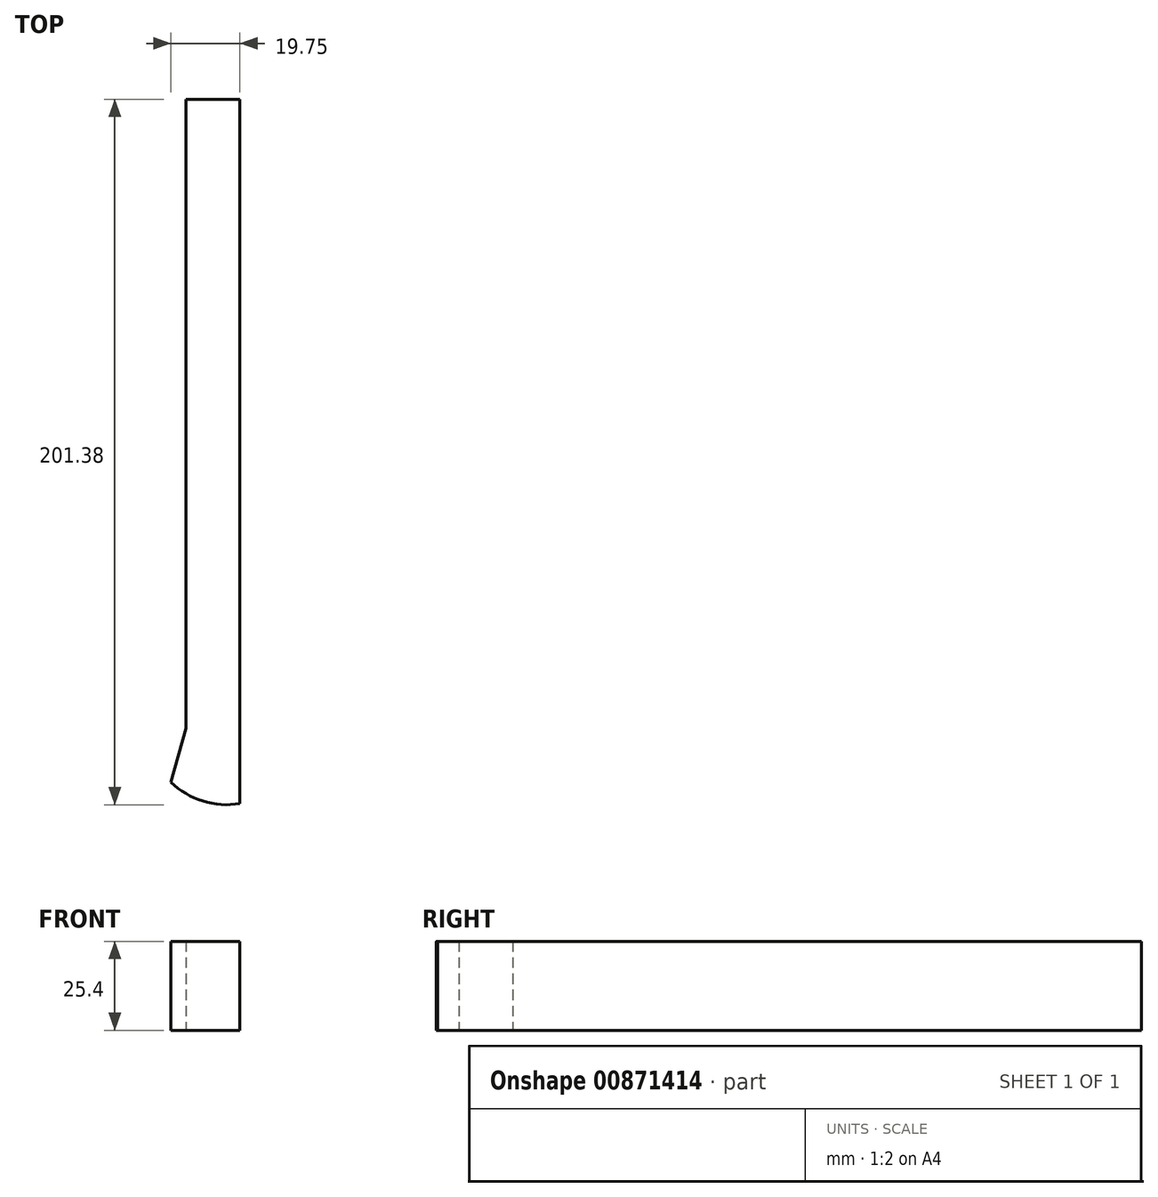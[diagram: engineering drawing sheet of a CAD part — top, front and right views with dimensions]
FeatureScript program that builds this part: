
annotation { "Feature Type Name" : "Feature", "Feature Type Description" : "" }
export const myFeature = defineFeature(function(context is Context, id is Id, definition is map)
    precondition{}
    {
        {
            var Q0;
            Q0=qCreatedBy(makeId("Top.planeOp"),FACE);
            var sketch = newSketch(context, id + "F0", { "sketchPlane" : qUnion([Q0])});
            skPoint(sketch, "E0.middle", {"position": v(0, 0) * mm});
            skLineSegment(sketch, "E1.bottom", {"start": v(-15.48, -23.78) * mm, "end": v(0, -23.78) * mm});
            skLineSegment(sketch, "E1.top", {"start": v(-15.48, -142.2) * mm, "end": v(0, -142.2) * mm});
            skLineSegment(sketch, "E1.left", {"start": v(-15.48, -23.78) * mm, "end": v(-15.48, -142.2) * mm});
            skLineSegment(sketch, "E1.right", {"start": v(0, -23.78) * mm, "end": v(0, -142.2) * mm});
            skLineSegment(sketch, "E2.top", {"start": v(-15.48, 48.59) * mm, "end": v(0, 48.59) * mm});
            skLineSegment(sketch, "E2.left", {"start": v(-15.48, -23.78) * mm, "end": v(-15.48, 48.59) * mm});
            skLineSegment(sketch, "E2.right", {"start": v(0, -23.78) * mm, "end": v(0, 48.59) * mm});
            skLineSegment(sketch, "E3", {"start": v(0, -142.2) * mm, "end": v(0, -152.47) * mm});
            skArc(sketch, "E4", {"start": v(-24.34, -140.03) * mm, "mid": v(-14.23, -150.29) * mm, "end": v(0, -152.47) * mm});
            skLineSegment(sketch, "E5", {"start": v(-15.48, -130.95) * mm, "end": v(-19.75, -146.34) * mm});
            skSolve(sketch);
        }
        {
            var Q0;
            {var subQ4=sQuery(id+"F0.wireOp",EDGE,"E1.top");Q0=makeQuery(id+"F0.imprint","IMPRINT",FACE,{"disambiguationData":[TD([[makeQuery(id+"F0.imprint","IMPRINT",EDGE,{"derivedFrom":subQ4}),-1.0]])]});}
            var Q1;
            {var subQ1=sQuery(id+"F0.wireOp",EDGE,"E1.top");Q1=makeQuery(id+"F0.imprint","IMPRINT",FACE,{"disambiguationData":[TD([[makeQuery(id+"F0.imprint","IMPRINT",EDGE,{"derivedFrom":subQ1}),1.0]])]});}
            var Q2;
            Q2=makeQuery(id+"F0.imprint","IMPRINT",FACE,{"disambiguationData":[TD([[makeQuery(id+"F0.imprint","IMPRINT",EDGE,{"derivedFrom":sQuery(id+"F0.wireOp",EDGE,"E1.bottom")}),1.0]])]});
            extrude(context, id + "F1", {"entities" : qUnion([Q0, Q1, Q2]), "depth" : 25.4 * mm, "offsetDistance" : 25.4 * mm});
        }
    });
